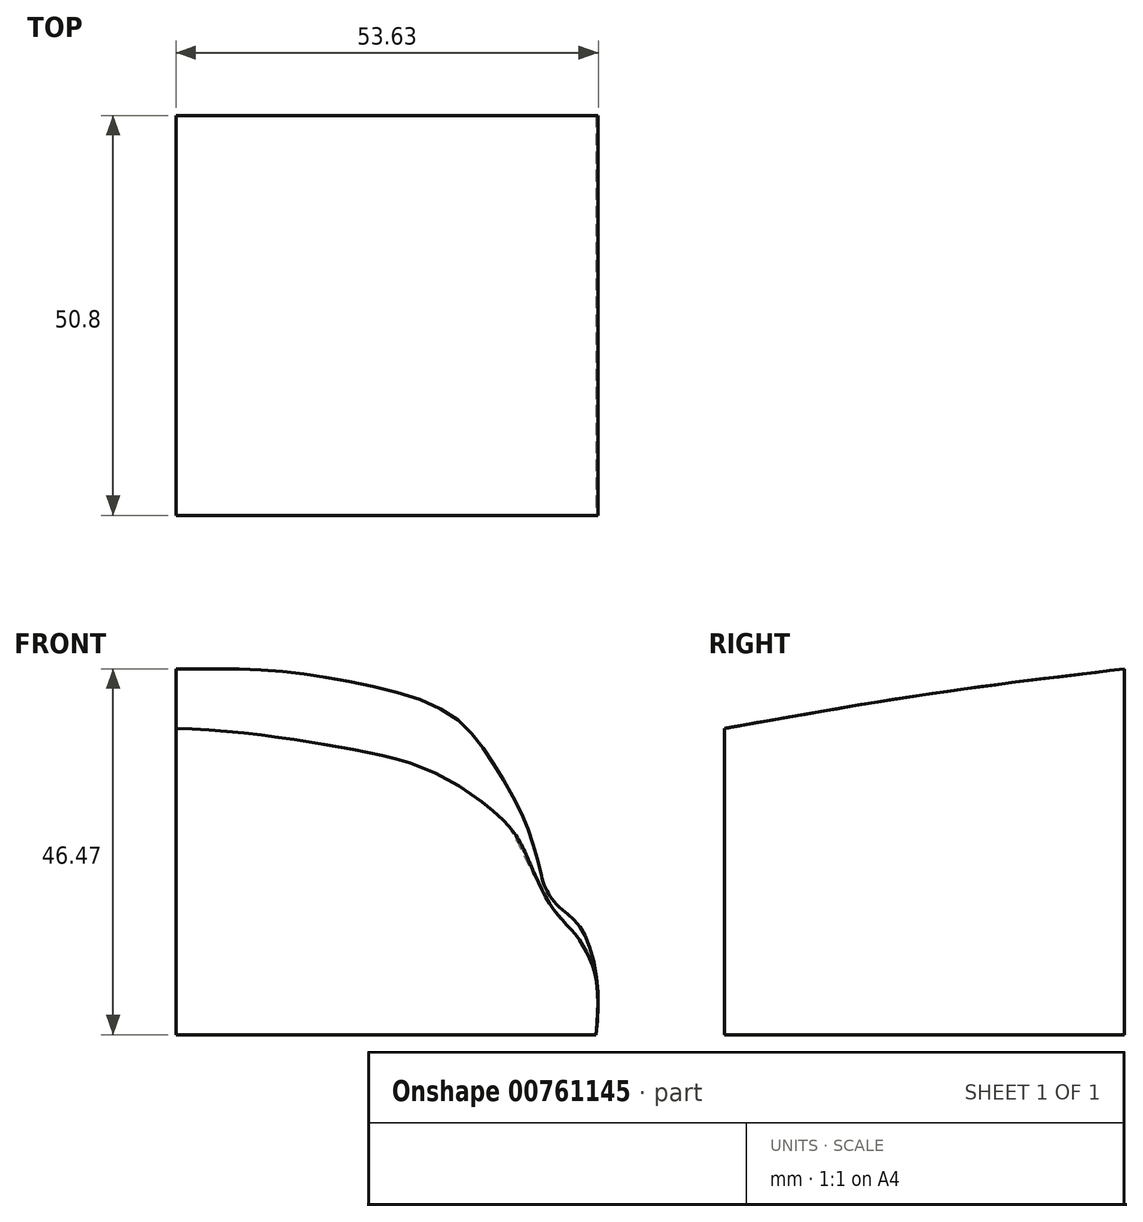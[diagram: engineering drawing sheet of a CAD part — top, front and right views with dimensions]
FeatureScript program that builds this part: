
annotation { "Feature Type Name" : "Feature", "Feature Type Description" : "" }
export const myFeature = defineFeature(function(context is Context, id is Id, definition is map)
    precondition{}
    {
        {
            var Q0;
            Q0=qCreatedBy(makeId("Front.planeOp"),FACE);
            var sketch = newSketch(context, id + "F0", { "sketchPlane" : qUnion([Q0])});
            skFitSpline(sketch, "E0", {"points": [v(53.36, 0) * mm, v(53.26, 8.3) * mm, v(51.25, 13.8) * mm, v(48.38, 16.49) * mm, v(45.07, 21.29) * mm, v(42.5, 27.06) * mm, v(38, 34.44) * mm, v(27.24, 40.81) * mm, v(11.37, 42.57) * mm, v(0, 43.18) * mm], "startDerivative": vector(11.02, 108.01) * mm, "endDerivative": vector(-84.7, -0.4) * mm});
            skLineSegment(sketch, "E1", {"start": v(53.36, 0) * mm, "end": v(0, 0) * mm});
            skLineSegment(sketch, "E2", {"start": v(0, 0) * mm, "end": v(0, 43.18) * mm});
            skSolve(sketch);
        }
        {
            var Q0;
            Q0=qCreatedBy(makeId("Front.planeOp"),FACE);
            cPlane(context, id + "F1", {"entities" : qUnion([Q0]), "cplaneType" : CPlaneType.OFFSET, "offset" : 25.4 * mm, "width" : 152.4 * mm, "height" : 152.4 * mm});
        }
        {
            var Q0;
            Q0=makeQuery(id+"F0.imprint","IMPRINT",FACE,{"disambiguationData":[TD([[makeQuery(id+"F0.imprint","IMPRINT",EDGE,{"derivedFrom":sQuery(id+"F0.wireOp",EDGE,"E0")}),1.0]])]});
            cPlane(context, id + "F2", {"entities" : qUnion([Q0]), "cplaneType" : CPlaneType.OFFSET, "offset" : 25.4 * mm, "oppositeDirection" : true, "width" : 152.4 * mm, "height" : 152.4 * mm});
        }
        {
            var Q0;
            Q0=qCreatedBy(id+"F1.planeOp",FACE);
            var sketch = newSketch(context, id + "F3", { "sketchPlane" : qUnion([Q0])});
            skFitSpline(sketch, "E3", {"points": [v(53.36, 0) * mm, v(53.1, 8.06) * mm, v(50.85, 12.57) * mm, v(47.91, 15.93) * mm, v(45.06, 21.5) * mm, v(42.55, 26.14) * mm, v(36.8, 31.01) * mm, v(30.05, 34.4) * mm, v(21.54, 36.4) * mm, v(12.03, 37.9) * mm, v(0, 38.9) * mm], "startDerivative": vector(9.51, 108.15) * mm, "endDerivative": vector(-84.7, 0.06) * mm});
            skLineSegment(sketch, "E4", {"start": v(53.36, 0) * mm, "end": v(0, 0) * mm});
            skLineSegment(sketch, "E5", {"start": v(0, 0) * mm, "end": v(0, 38.9) * mm});
            skSolve(sketch);
        }
        {
            var Q0;
            Q0=qCreatedBy(id+"F2.planeOp",FACE);
            var sketch = newSketch(context, id + "F4", { "sketchPlane" : qUnion([Q0])});
            skFitSpline(sketch, "E6", {"points": [v(53.36, 0) * mm, v(53.1, 8.06) * mm, v(50.85, 12.57) * mm, v(47.91, 15.93) * mm, v(46.1, 21.45) * mm, v(44.22, 27.32) * mm, v(40.22, 34.58) * mm, v(34.6, 40.83) * mm, v(22.09, 44.84) * mm, v(10.58, 46.34) * mm, v(0, 46.46) * mm], "startDerivative": vector(9.51, 108.15) * mm, "endDerivative": vector(-84.7, 0.06) * mm});
            skLineSegment(sketch, "E7", {"start": v(53.36, 0) * mm, "end": v(0, 0) * mm});
            skLineSegment(sketch, "E8", {"start": v(0, 0) * mm, "end": v(0, 46.46) * mm});
            skSolve(sketch);
        }
        {
            var Q0;
            Q0=makeQuery(id+"F4.imprint","IMPRINT",FACE,{"disambiguationData":[TD([[makeQuery(id+"F4.imprint","IMPRINT",EDGE,{"derivedFrom":sQuery(id+"F4.wireOp",EDGE,"E6")}),1.0]])]});
            var Q1;
            Q1=makeQuery(id+"F0.imprint","IMPRINT",FACE,{"disambiguationData":[TD([[makeQuery(id+"F0.imprint","IMPRINT",EDGE,{"derivedFrom":sQuery(id+"F0.wireOp",EDGE,"E0")}),1.0]])]});
            var Q2;
            Q2=makeQuery(id+"F3.imprint","IMPRINT",FACE,{"disambiguationData":[TD([[makeQuery(id+"F3.imprint","IMPRINT",EDGE,{"derivedFrom":sQuery(id+"F3.wireOp",EDGE,"E3")}),1.0]])]});
            loft(context, id + "F5", {"sheetProfilesArray" : [{ "sheetProfileEntities" : qUnion([Q0]) }, { "sheetProfileEntities" : qUnion([Q1]) }, { "sheetProfileEntities" : qUnion([Q2]) }]});
        }
    });
